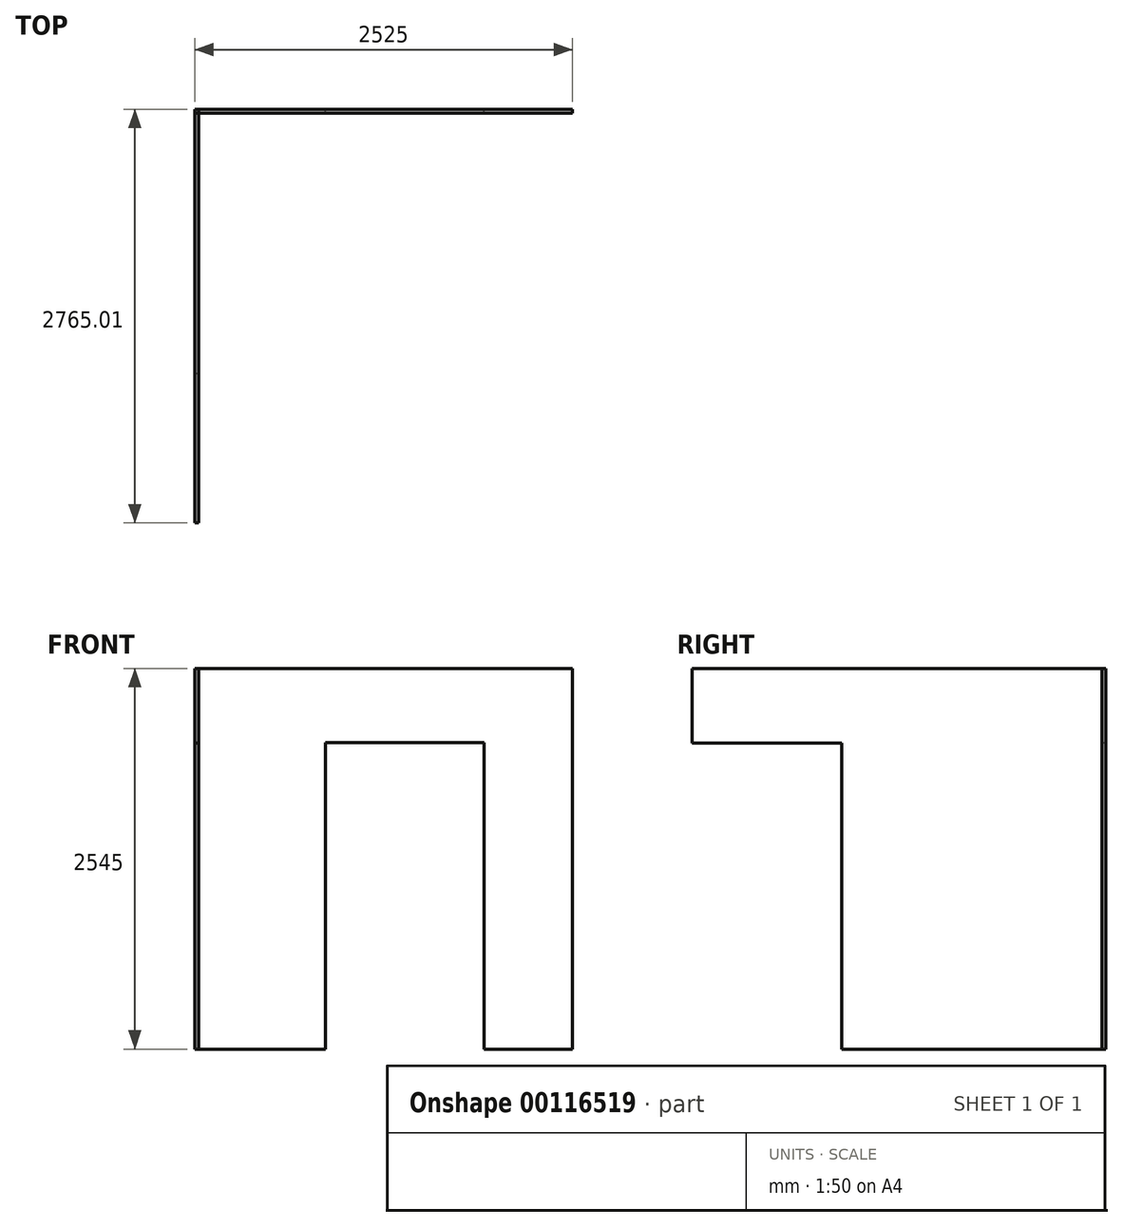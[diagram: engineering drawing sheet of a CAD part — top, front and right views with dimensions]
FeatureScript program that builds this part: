
annotation { "Feature Type Name" : "Feature", "Feature Type Description" : "" }
export const myFeature = defineFeature(function(context is Context, id is Id, definition is map)
    precondition{}
    {
        {
            var Q0;
            Q0=qCreatedBy(makeId("Front.planeOp"),FACE);
            var sketch = newSketch(context, id + "F0", { "sketchPlane" : qUnion([Q0])});
            skLineSegment(sketch, "E0", {"start": v(-1609.07, 1275.17) * mm, "end": v(890.93, 1275.17) * mm});
            skLineSegment(sketch, "E1", {"start": v(890.93, 1275.17) * mm, "end": v(890.93, -1269.83) * mm});
            skLineSegment(sketch, "E2", {"start": v(890.93, -1269.83) * mm, "end": v(300.93, -1269.83) * mm});
            skLineSegment(sketch, "E3", {"start": v(300.93, -1269.83) * mm, "end": v(300.93, 780.17) * mm});
            skLineSegment(sketch, "E4", {"start": v(300.93, 780.17) * mm, "end": v(-759.07, 780.17) * mm});
            skLineSegment(sketch, "E5", {"start": v(-759.07, 780.17) * mm, "end": v(-759.07, -1269.83) * mm});
            skLineSegment(sketch, "E6", {"start": v(-759.07, -1269.83) * mm, "end": v(-1609.07, -1269.83) * mm});
            skLineSegment(sketch, "E7", {"start": v(-1609.07, -1269.83) * mm, "end": v(-1609.07, 1275.17) * mm});
            skSolve(sketch);
        }
        {
            var Q0;
            Q0 = qSketchRegion(id + "F0", true);
            extrude(context, id + "F1", {"entities" : qUnion([Q0]), "depth" : 25 * mm});
        }
        {
            var Q0;
            Q0=makeQuery(id+"F1.opExtrude","SWEPT_FACE",FACE,{"disambiguationData":[OSD([sQuery(id+"F0.wireOp",EDGE,"E7")])]});
            var sketch = newSketch(context, id + "F2", { "sketchPlane" : qUnion([Q0])});
            skLineSegment(sketch, "E8.bottom", {"start": v(25, 1275.17) * mm, "end": v(1043, 1275.17) * mm});
            skLineSegment(sketch, "E8.top", {"start": v(25, -1269.83) * mm, "end": v(1043, -1269.83) * mm});
            skLineSegment(sketch, "E8.left", {"start": v(25, 1275.17) * mm, "end": v(25, -1269.83) * mm});
            skLineSegment(sketch, "E8.right", {"start": v(1043, 1275.17) * mm, "end": v(1043, -1269.83) * mm});
            skSolve(sketch);
        }
        {
            var Q0;
            Q0=makeQuery(id+"F2.imprint","IMPRINT",FACE,{"disambiguationData":[TD([[makeQuery(id+"F2.imprint","IMPRINT",EDGE,{"derivedFrom":sQuery(id+"F2.wireOp",EDGE,"E8.bottom")}),-1.0]])]});
            extrude(context, id + "F3", {"entities" : qUnion([Q0]), "depth" : 25 * mm});
        }
        {
            var Q0;
            Q0=makeQuery(id+"F1.opExtrude","SWEPT_FACE",FACE,{"disambiguationData":[OSD([sQuery(id+"F0.wireOp",EDGE,"E7")])]});
            extrude(context, id + "F4", {"entities" : qUnion([Q0]), "depth" : 25 * mm});
        }
        {
            var Q0;
            Q0=makeQuery(id+"F3.opExtrude","SWEPT_FACE",FACE,{"disambiguationData":[OSD([sQuery(id+"F2.wireOp",EDGE,"E8.right")])]});
            extrude(context, id + "F5", {"entities" : qUnion([Q0]), "operationType" : NewBodyOperationType.ADD, "depth" : 722 * mm});
        }
        {
            var Q0;
            Q0=makeQuery(id+"F5.opExtrude","CAP_FACE",FACE,{"disambiguationData":[OSD([sQuery(id+"F2.wireOp",EDGE,"E8.right")])],"isStart":false});
            var sketch = newSketch(context, id + "F6", { "sketchPlane" : qUnion([Q0])});
            skLineSegment(sketch, "E9.bottom", {"start": v(-1634.07, 1275.17) * mm, "end": v(-1609.07, 1275.17) * mm});
            skLineSegment(sketch, "E9.top", {"start": v(-1634.07, 775.34) * mm, "end": v(-1609.07, 775.34) * mm});
            skLineSegment(sketch, "E9.left", {"start": v(-1634.07, 1275.17) * mm, "end": v(-1634.07, 775.34) * mm});
            skLineSegment(sketch, "E9.right", {"start": v(-1609.07, 1275.17) * mm, "end": v(-1609.07, 775.34) * mm});
            skSolve(sketch);
        }
        {
            var Q0;
            Q0=makeQuery(id+"F6.imprint","IMPRINT",FACE,{"disambiguationData":[TD([[makeQuery(id+"F6.imprint","IMPRINT",EDGE,{"derivedFrom":sQuery(id+"F6.wireOp",EDGE,"E9.bottom")}),-1.0]])]});
            extrude(context, id + "F7", {"entities" : qUnion([Q0]), "operationType" : NewBodyOperationType.ADD, "depth" : 1000 * mm});
        }
    });
